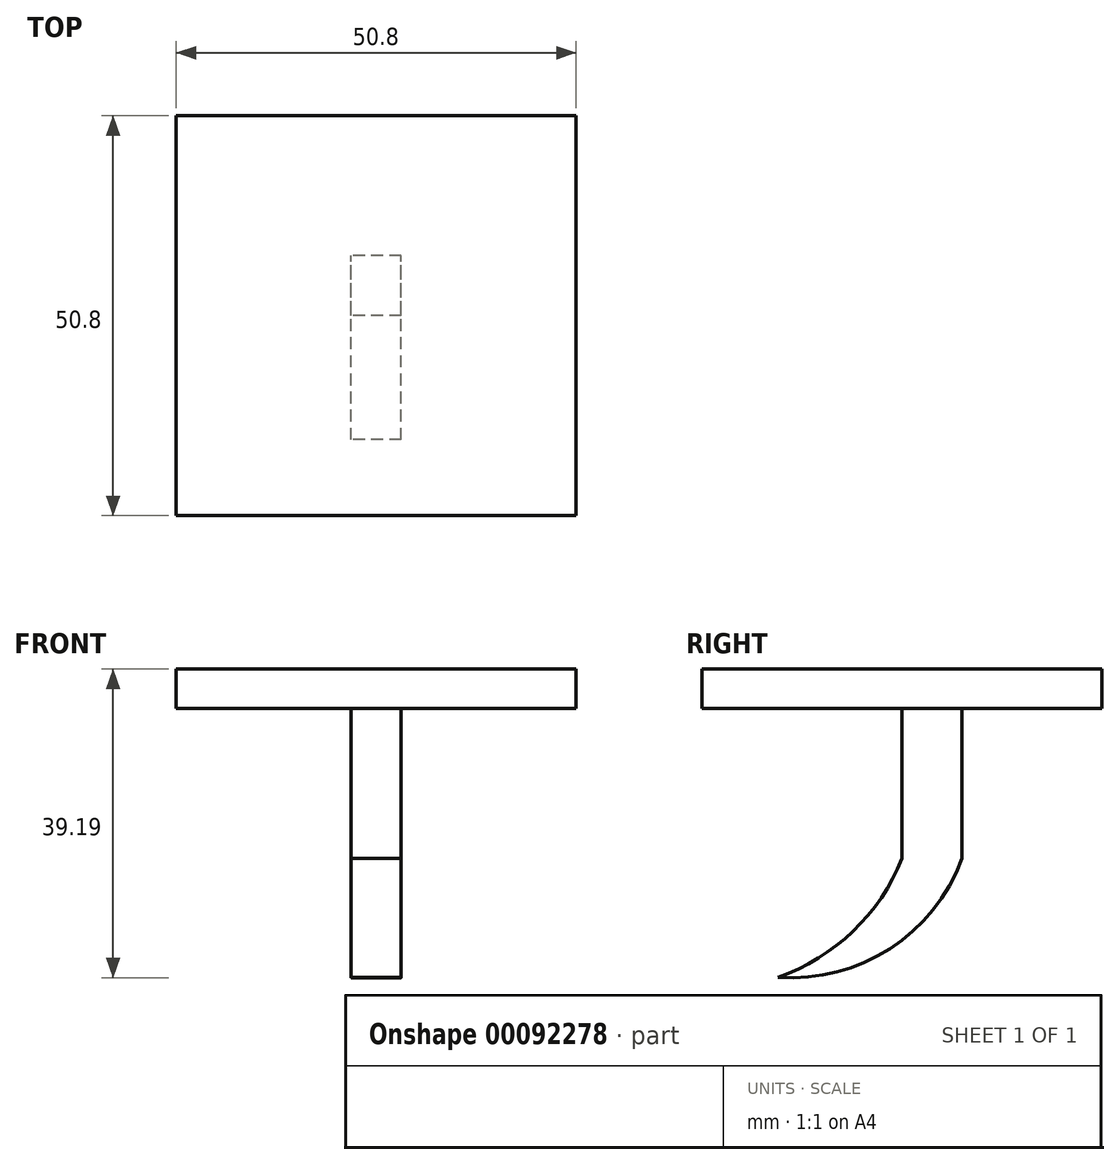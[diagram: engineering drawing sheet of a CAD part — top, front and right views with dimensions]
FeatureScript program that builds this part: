
annotation { "Feature Type Name" : "Feature", "Feature Type Description" : "" }
export const myFeature = defineFeature(function(context is Context, id is Id, definition is map)
    precondition{}
    {
        {
            var Q0;
            Q0=qCreatedBy(makeId("Top.planeOp"),FACE);
            var sketch = newSketch(context, id + "F0", { "sketchPlane" : qUnion([Q0])});
            skLineSegment(sketch, "E0.bottom", {"start": v(25.4, 25.4) * mm, "end": v(-25.4, 25.4) * mm});
            skLineSegment(sketch, "E0.top", {"start": v(25.4, -25.4) * mm, "end": v(-25.4, -25.4) * mm});
            skLineSegment(sketch, "E0.left", {"start": v(25.4, 25.4) * mm, "end": v(25.4, -25.4) * mm});
            skLineSegment(sketch, "E0.right", {"start": v(-25.4, 25.4) * mm, "end": v(-25.4, -25.4) * mm});
            skPoint(sketch, "E0.middle", {"position": v(0, 0) * mm});
            skSolve(sketch);
        }
        {
            var Q0;
            Q0 = qSketchRegion(id + "F0", true);
            extrude(context, id + "F1", {"entities" : qUnion([Q0]), "depth" : 5 * mm});
        }
        {
            var Q0;
            Q0=qCreatedBy(makeId("Right.planeOp"),FACE);
            var sketch = newSketch(context, id + "F2", { "sketchPlane" : qUnion([Q0])});
            skLineSegment(sketch, "E1.bottom", {"start": v(0, 0) * mm, "end": v(7.62, 0) * mm});
            skLineSegment(sketch, "E1.top", {"start": v(0, -19.05) * mm, "end": v(7.62, -19.05) * mm});
            skLineSegment(sketch, "E1.left", {"start": v(0, 0) * mm, "end": v(0, -19.05) * mm});
            skLineSegment(sketch, "E1.right", {"start": v(7.62, 0) * mm, "end": v(7.62, -19.05) * mm});
            skArc(sketch, "E2", {"start": v(-15.74, -34.13) * mm, "mid": v(-1.53, -30.5) * mm, "end": v(7.62, -19.05) * mm});
            skArc(sketch, "E3", {"start": v(-15.74, -34.13) * mm, "mid": v(-6.24, -28.3) * mm, "end": v(0, -19.05) * mm});
            skSolve(sketch);
        }
        {
            var Q0;
            Q0=makeQuery(id+"F2.imprint","IMPRINT",FACE,{"disambiguationData":[TD([[makeQuery(id+"F2.imprint","IMPRINT",EDGE,{"derivedFrom":sQuery(id+"F2.wireOp",EDGE,"E1.bottom")}),-1.0]])]});
            var Q1;
            Q1=makeQuery(id+"F2.imprint","IMPRINT",FACE,{"disambiguationData":[TD([[makeQuery(id+"F2.imprint","IMPRINT",EDGE,{"derivedFrom":sQuery(id+"F2.wireOp",EDGE,"E1.top")}),-1.0]])]});
            extrude(context, id + "F3", {"entities" : qUnion([Q0, Q1]), "operationType" : NewBodyOperationType.ADD, "depth" : 3.17 * mm});
        }
        {
            var Q0;
            Q0=makeQuery(id+"F3.opExtrude","CAP_FACE",FACE,{"disambiguationData":[OSD([sQuery(id+"F2.wireOp",EDGE,"E1.bottom"),sQuery(id+"F2.wireOp",EDGE,"E1.left"),sQuery(id+"F2.wireOp",EDGE,"E1.right"),sQuery(id+"F2.wireOp",EDGE,"E2"),sQuery(id+"F2.wireOp",EDGE,"E3")])],"isStart":true});
            extrude(context, id + "F4", {"entities" : qUnion([Q0]), "operationType" : NewBodyOperationType.ADD, "depth" : 3.17 * mm});
        }
    });
